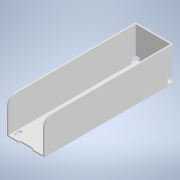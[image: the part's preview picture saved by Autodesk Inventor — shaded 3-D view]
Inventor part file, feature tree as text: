
AUTODESK INVENTOR PART (.ipt)
format: ipt  version: 2022 (Build 260153000, 153)  size: 233,472 bytes
history: native  units: mm
features: extrude x12, sketch x12, other x3, fillet x2, reference x1, projected_geometry x1
ambient origin geometry x8: Origin, YZ Plane, XZ Plane, XY Plane, X Axis, Y Axis, Z Axis, Center Point
bodies: Solid1 (feature_tree)
feature tree (31):
  extrude  "Extrusion1"  Depth=15.7mm
  extrude  "Extrusion2"  Depth=3.0mm TaperAngle=0.0deg
  extrude  "Extrusion3"  Depth=3.0mm TaperAngle=0.0deg
  fillet  "Fillet1"  Radius=63.5mm
  extrude  "Extrusion4"  Depth=20.0mm
  fillet  "Fillet2"  Radius=63.5mm
  extrude  "Extrusion5"  Depth=3.0mm TaperAngle=0.0deg
  extrude  "Extrusion6"  Depth=3.0mm TaperAngle=0.0deg
  extrude  "Extrusion7"  Depth=12.515mm
  extrude  "Extrusion8"  Depth=3.0mm TaperAngle=0.0deg
  extrude  "Extrusion9"  Depth=3.0mm TaperAngle=0.0deg
  extrude  "Extrusion11"  Depth=12.515mm
  extrude  "Extrusion12"  Depth=3.0mm TaperAngle=0.0deg
  extrude  "Extrusion13"  Depth=3.0mm TaperAngle=0.0deg
  sketch  "Sketch1"  dims[d0=87.28mm d1=15.7mm]
  sketch  "Sketch2"  dims[d2=15.7mm d3=3.0mm d4=0.0mm]
  sketch  "Sketch3"  dims[d5=297.64mm d6=3.0mm d7=0.0mm d8=63.5mm]
  sketch  "Sketch4"  dims[d9=3.0mm d10=0.0mm d11=20.0mm d12=63.5mm]
  sketch  "Sketch5"  dims[d13=3.0mm d14=3.0mm d15=0.0mm]
  sketch  "Sketch6"  dims[d16=20.0mm d17=3.0mm d18=0.0mm]
  sketch  "Sketch7"  dims[d19=3.0mm d20=12.515mm]
  sketch  "Sketch8"  dims[d21=12.7mm d22=3.0mm d23=0.0mm]
  sketch  "Sketch9"  dims[d24=9.515mm d25=3.0mm d26=0.0mm]
  sketch  "Sketch11"  dims[d27=3.0mm d28=12.515mm]
  reference  "Reference1"
  sketch  "Sketch12"  dims[d29=12.7mm d30=3.0mm d31=0.0mm]
  sketch  "Sketch13"  dims[d32=3.0mm d33=0.0mm d48=3.0mm d49=0.0mm d50=10.0mm d51=0.0mm d52=0.5mm d53=0.5mm d54=0.0mm d55=3.0mm d56=30.0mm d57=28.64mm d58=3.0mm d59=0.0mm]
  projected_geometry  "Projected Loop1"
  other  "<userpath>\OneDrive\Desktop\P3\2. Hopper Assembly\Hopper_And_Connecting_Plate.iam"
  other  "Hopper_And_Connecting_Plate.iam"
  other  "Hopper1:1"
